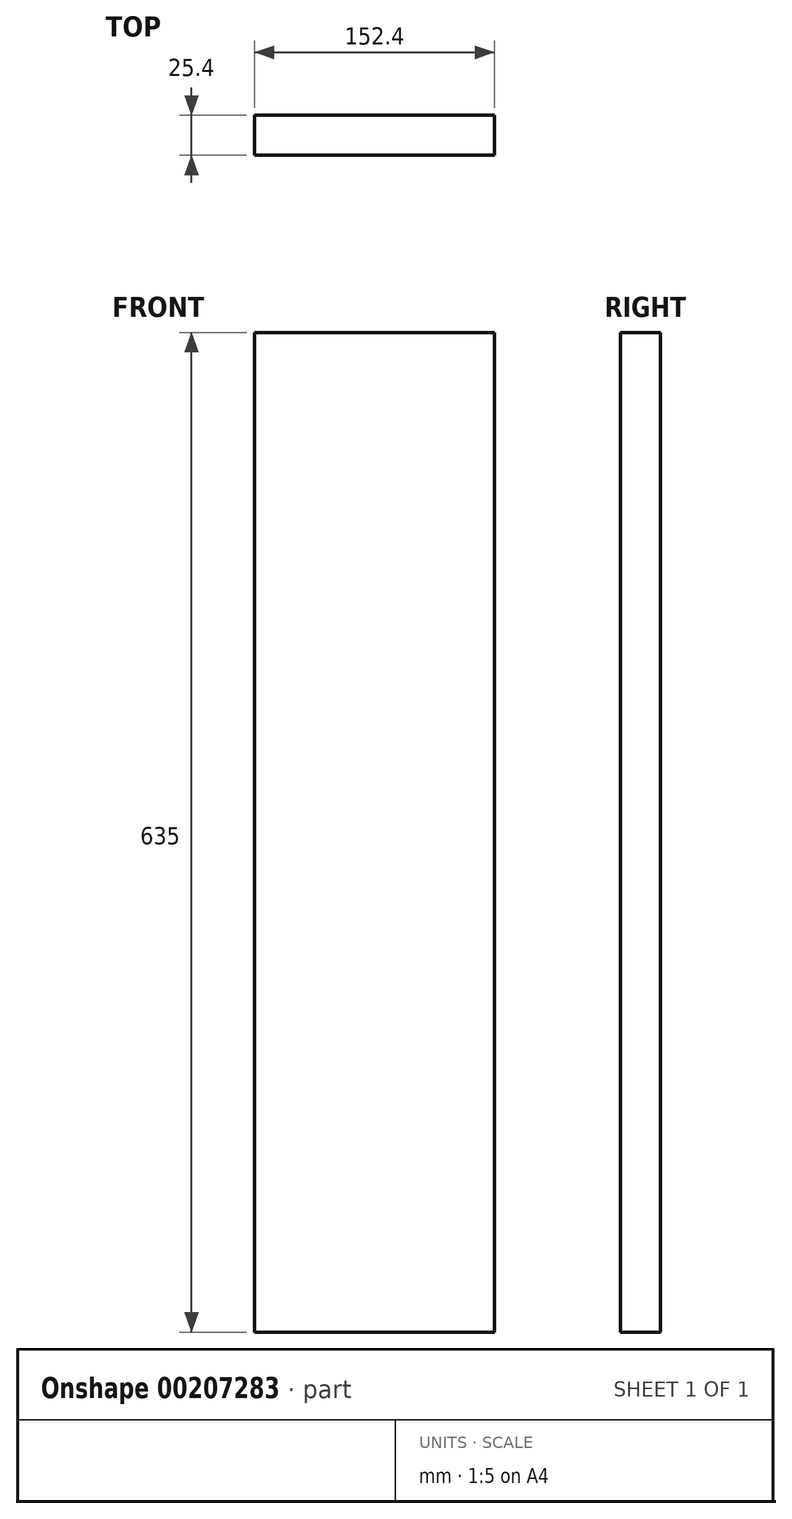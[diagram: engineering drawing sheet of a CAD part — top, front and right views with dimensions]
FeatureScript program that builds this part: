
annotation { "Feature Type Name" : "Feature", "Feature Type Description" : "" }
export const myFeature = defineFeature(function(context is Context, id is Id, definition is map)
    precondition{}
    {
        {
            var Q0;
            Q0=qCreatedBy(makeId("Front.planeOp"),FACE);
            var sketch = newSketch(context, id + "F0", { "sketchPlane" : qUnion([Q0])});
            skLineSegment(sketch, "E0.bottom", {"start": v(76.2, -317.5) * mm, "end": v(-76.2, -317.5) * mm});
            skLineSegment(sketch, "E0.top", {"start": v(76.2, 317.5) * mm, "end": v(-76.2, 317.5) * mm});
            skLineSegment(sketch, "E0.left", {"start": v(76.2, -317.5) * mm, "end": v(76.2, 317.5) * mm});
            skLineSegment(sketch, "E0.right", {"start": v(-76.2, -317.5) * mm, "end": v(-76.2, 317.5) * mm});
            skPoint(sketch, "E0.middle", {"position": v(0, 0) * mm});
            skSolve(sketch);
        }
        {
            var Q0;
            Q0=makeQuery(id+"F0.imprint","IMPRINT",FACE,{"disambiguationData":[TD([[makeQuery(id+"F0.imprint","IMPRINT",EDGE,{"derivedFrom":sQuery(id+"F0.wireOp",EDGE,"E0.bottom")}),-1.0]])]});
            extrude(context, id + "F1", {"entities" : qUnion([Q0]), "depth" : 25.4 * mm});
        }
    });
